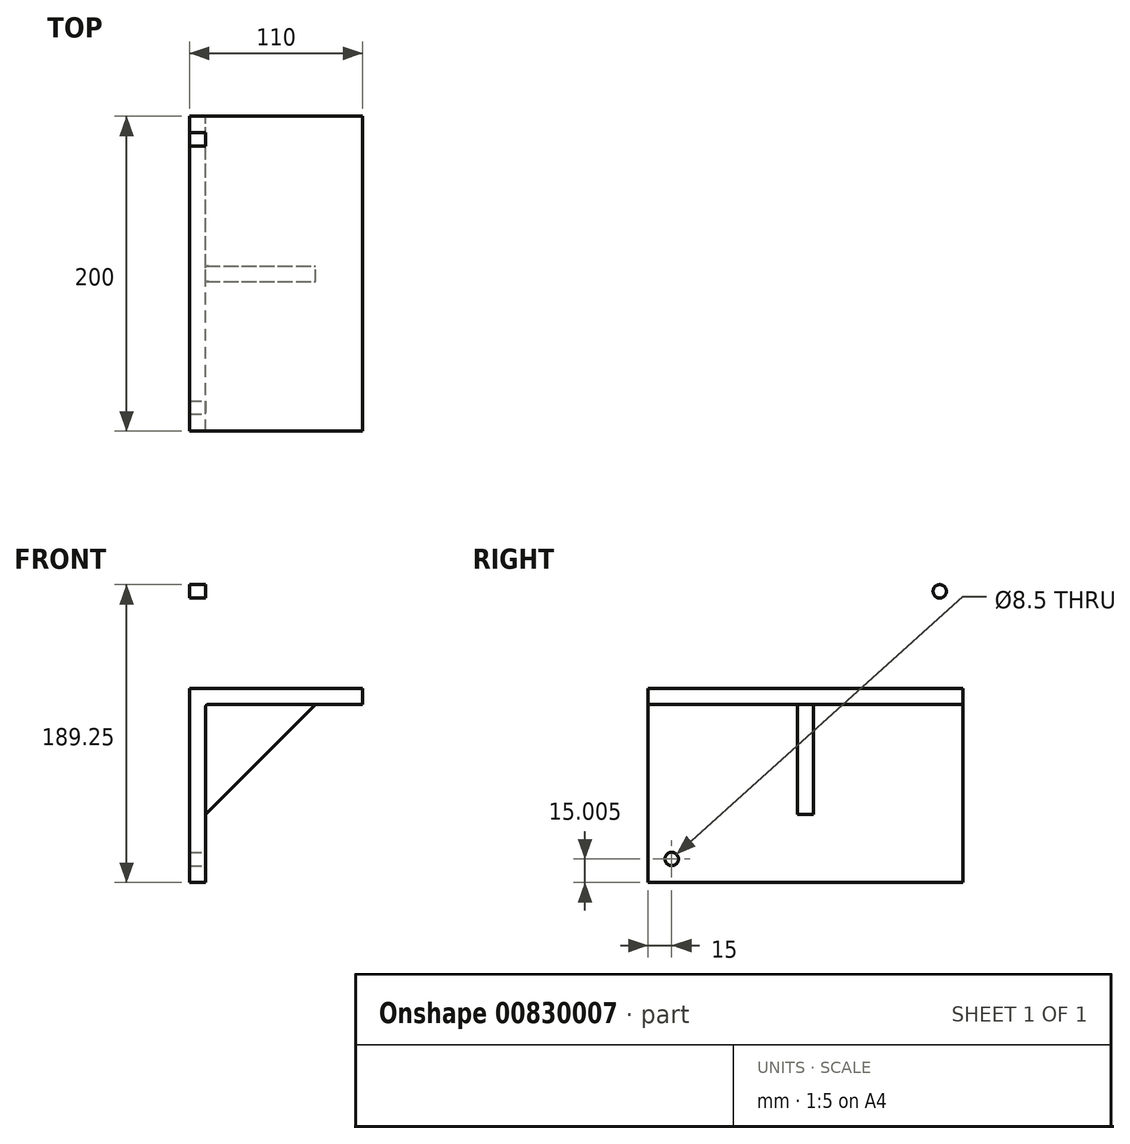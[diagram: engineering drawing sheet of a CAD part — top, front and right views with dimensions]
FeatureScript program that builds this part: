
annotation { "Feature Type Name" : "Feature", "Feature Type Description" : "" }
export const myFeature = defineFeature(function(context is Context, id is Id, definition is map)
    precondition{}
    {
        {
            var Q0;
            Q0=qCreatedBy(makeId("Front.planeOp"),FACE);
            var sketch = newSketch(context, id + "F0", { "sketchPlane" : qUnion([Q0])});
            skLineSegment(sketch, "E0", {"start": v(-10, 154.16) * mm, "end": v(0, 154.16) * mm});
            skLineSegment(sketch, "E1", {"start": v(0, 154.16) * mm, "end": v(0, 77.36) * mm});
            skLineSegment(sketch, "E2", {"start": v(-10, 154.16) * mm, "end": v(-10, -45.84) * mm});
            skLineSegment(sketch, "E3", {"start": v(-10, -45.84) * mm, "end": v(0, -45.84) * mm});
            skLineSegment(sketch, "E4", {"start": v(0, -45.84) * mm, "end": v(0, 67.36) * mm});
            skLineSegment(sketch, "E5", {"start": v(0, 77.36) * mm, "end": v(100, 77.36) * mm});
            skLineSegment(sketch, "E6", {"start": v(100, 77.36) * mm, "end": v(100, 67.36) * mm});
            skLineSegment(sketch, "E7", {"start": v(0, 67.36) * mm, "end": v(100, 67.36) * mm});
            skLineSegment(sketch, "E8", {"start": v(0, 67.36) * mm, "end": v(70, 67.36) * mm});
            skLineSegment(sketch, "E9", {"start": v(0, 67.36) * mm, "end": v(0, -2.64) * mm});
            skLineSegment(sketch, "E10", {"start": v(0, -2.64) * mm, "end": v(70, 67.36) * mm});
            skSolve(sketch);
        }
        {
            var Q0;
            Q0=makeQuery(id+"F0.imprint","IMPRINT",FACE,{"disambiguationData":[TD([[makeQuery(id+"F0.imprint","IMPRINT",EDGE,{"derivedFrom":sQuery(id+"F0.wireOp",EDGE,"E0")}),-1.0]])]});
            extrude(context, id + "F1", {"entities" : qUnion([Q0]), "depth" : 100 * mm, "offsetDistance" : 25 * mm});
        }
        {
            var Q0;
            Q0=makeQuery(id+"F0.imprint","IMPRINT",FACE,{"disambiguationData":[TD([[makeQuery(id+"F0.imprint","IMPRINT",EDGE,{"derivedFrom":sQuery(id+"F0.wireOp",EDGE,"E0")}),-1.0]])]});
            extrude(context, id + "F2", {"entities" : qUnion([Q0]), "operationType" : NewBodyOperationType.ADD, "oppositeDirection" : true, "depth" : 100 * mm, "offsetDistance" : 25 * mm});
        }
        {
            var Q0;
            {var subQ0=sQuery(id+"F0.wireOp",EDGE,"E10");Q0=makeQuery(id+"F0.imprint","IMPRINT",FACE,{"disambiguationData":[TD([[makeQuery(id+"F0.imprint","IMPRINT",EDGE,{"derivedFrom":subQ0}),1.0]])]});}
            extrude(context, id + "F3", {"entities" : qUnion([Q0]), "operationType" : NewBodyOperationType.ADD, "depth" : 5 * mm, "offsetDistance" : 25 * mm});
        }
        {
            var Q0;
            {var subQ0=sQuery(id+"F0.wireOp",EDGE,"E10");Q0=makeQuery(id+"F0.imprint","IMPRINT",FACE,{"disambiguationData":[TD([[makeQuery(id+"F0.imprint","IMPRINT",EDGE,{"derivedFrom":subQ0}),1.0]])]});}
            extrude(context, id + "F4", {"entities" : qUnion([Q0]), "operationType" : NewBodyOperationType.ADD, "oppositeDirection" : true, "depth" : 5 * mm, "offsetDistance" : 25 * mm});
        }
        {
            var Q0;
            {var subQ0=sQuery(id+"F0.wireOp",EDGE,"E1");Q0=makeQuery(id+"F2.boolean.opBoolean","MERGE",FACE,{"derivedFrom":[makeQuery(id+"F1.opExtrude","SWEPT_FACE",FACE,{"disambiguationData":[OSD([subQ0])]}),makeQuery(id+"F2.opExtrude","SWEPT_FACE",FACE,{"disambiguationData":[OSD([subQ0])]})]});}
            var sketch = newSketch(context, id + "F5", { "sketchPlane" : qUnion([Q0])});
            skCircle(sketch, "E11", {"center": v(-85.26, 139.16) * mm, "radius": 4.25 * mm});
            skCircle(sketch, "E12.MirrorC", {"center": v(85.26, 139.16) * mm, "radius": 4.25 * mm});
            skCircle(sketch, "E13", {"center": v(-85, -30.84) * mm, "radius": 4.25 * mm});
            skCircle(sketch, "E14.MirrorC", {"center": v(85, -30.84) * mm, "radius": 4.25 * mm});
            skSolve(sketch);
        }
        {
            var Q0;
            Q0=makeQuery(id+"F5.imprint","IMPRINT",FACE,{"disambiguationData":[TD([[makeQuery(id+"F5.imprint","IMPRINT",EDGE,{"derivedFrom":sQuery(id+"F5.wireOp",EDGE,"E12.MirrorC")}),-1.0]])]});
            var Q1;
            Q1=makeQuery(id+"F5.imprint","IMPRINT",FACE,{"disambiguationData":[TD([[makeQuery(id+"F5.imprint","IMPRINT",EDGE,{"derivedFrom":sQuery(id+"F5.wireOp",EDGE,"E11")}),1.0]])]});
            var Q2;
            Q2=makeQuery(id+"F5.imprint","IMPRINT",FACE,{"disambiguationData":[TD([[makeQuery(id+"F5.imprint","IMPRINT",EDGE,{"derivedFrom":sQuery(id+"F5.wireOp",EDGE,"E13")}),1.0]])]});
            var Q3;
            Q3=makeQuery(id+"F5.imprint","IMPRINT",FACE,{"disambiguationData":[TD([[makeQuery(id+"F5.imprint","IMPRINT",EDGE,{"derivedFrom":sQuery(id+"F5.wireOp",EDGE,"E14.MirrorC")}),-1.0]])]});
            extrude(context, id + "F6", {"entities" : qUnion([Q0, Q1, Q2, Q3]), "operationType" : NewBodyOperationType.REMOVE, "oppositeDirection" : true, "depth" : 10 * mm, "offsetDistance" : 25 * mm});
        }
        {
            var Q0;
            {var subQ0=sQuery(id+"F0.wireOp",EDGE,"E7");var subQ1=sQuery(id+"F0.wireOp",EDGE,"E4");Q0=makeQuery(id+"F3.boolean.opBoolean","SPLIT",EDGE,{"disambiguationData":[TD([makeQuery(id+"F3.opExtrude","CAP_FACE",FACE,{"disambiguationData":[OSD([subQ1,subQ0,sQuery(id+"F0.wireOp",EDGE,"E10")])],"isStart":false})])],"derivedFrom":makeQuery(id+"F2.boolean.opBoolean","MERGE",EDGE,{"derivedFrom":[makeQuery(id+"F1.opExtrude","SWEPT_EDGE",EDGE,{"disambiguationData":[OSD([subQ1,subQ0])]}),makeQuery(id+"F2.opExtrude","SWEPT_EDGE",EDGE,{"disambiguationData":[OSD([subQ1,subQ0])]})]})});}
            var Q1;
            {var subQ0=sQuery(id+"F0.wireOp",EDGE,"E4");var subQ1=sQuery(id+"F0.wireOp",EDGE,"E7");Q1=makeQuery(id+"F3.boolean.opBoolean","SPLIT",EDGE,{"disambiguationData":[TD([makeQuery(id+"F3.opExtrude","CAP_FACE",FACE,{"disambiguationData":[OSD([subQ0,subQ1,sQuery(id+"F0.wireOp",EDGE,"E10")])],"isStart":true})])],"derivedFrom":makeQuery(id+"F2.boolean.opBoolean","MERGE",EDGE,{"derivedFrom":[makeQuery(id+"F1.opExtrude","SWEPT_EDGE",EDGE,{"disambiguationData":[OSD([subQ0,subQ1])]}),makeQuery(id+"F2.opExtrude","SWEPT_EDGE",EDGE,{"disambiguationData":[OSD([subQ0,subQ1])]})]})});}
            var Q2;
            Q2=makeQuery(id+"F4.opExtrude","CAP_EDGE",EDGE,{"disambiguationData":[OSD([sQuery(id+"F0.wireOp",EDGE,"E4")])],"isStart":false});
            var Q3;
            Q3=makeQuery(id+"F4.opExtrude","CAP_EDGE",EDGE,{"disambiguationData":[OSD([sQuery(id+"F0.wireOp",EDGE,"E7")])],"isStart":false});
            var Q4;
            Q4=makeQuery(id+"F3.opExtrude","CAP_EDGE",EDGE,{"disambiguationData":[OSD([sQuery(id+"F0.wireOp",EDGE,"E7")])],"isStart":false});
            var Q5;
            Q5=makeQuery(id+"F3.opExtrude","CAP_EDGE",EDGE,{"disambiguationData":[OSD([sQuery(id+"F0.wireOp",EDGE,"E4")])],"isStart":false});
            var Q6;
            {var subQ0=sQuery(id+"F0.wireOp",EDGE,"E10");var subQ1=sQuery(id+"F0.wireOp",EDGE,"E4");Q6=makeQuery(id+"F4.boolean.opBoolean","MERGE",EDGE,{"derivedFrom":[makeQuery(id+"F3.opExtrude","SWEPT_EDGE",EDGE,{"disambiguationData":[OSD([subQ1,subQ0])]}),makeQuery(id+"F4.opExtrude","SWEPT_EDGE",EDGE,{"disambiguationData":[OSD([subQ1,subQ0])]})]});}
            var Q7;
            {var subQ0=sQuery(id+"F0.wireOp",EDGE,"E10");var subQ1=sQuery(id+"F0.wireOp",EDGE,"E7");Q7=makeQuery(id+"F4.boolean.opBoolean","MERGE",EDGE,{"derivedFrom":[makeQuery(id+"F3.opExtrude","SWEPT_EDGE",EDGE,{"disambiguationData":[OSD([subQ1,subQ0])]}),makeQuery(id+"F4.opExtrude","SWEPT_EDGE",EDGE,{"disambiguationData":[OSD([subQ1,subQ0])]})]});}
            var Q8;
            {var subQ0=sQuery(id+"F0.wireOp",EDGE,"E5");var subQ1=sQuery(id+"F0.wireOp",EDGE,"E1");Q8=makeQuery(id+"F2.boolean.opBoolean","MERGE",EDGE,{"derivedFrom":[makeQuery(id+"F1.opExtrude","SWEPT_EDGE",EDGE,{"disambiguationData":[OSD([subQ1,subQ0])]}),makeQuery(id+"F2.opExtrude","SWEPT_EDGE",EDGE,{"disambiguationData":[OSD([subQ1,subQ0])]})]});}
            fillet(context, id + "F7", {"entities" : qUnion([Q0, Q1, Q2, Q3, Q4, Q5, Q6, Q7, Q8]), "radius" : 2 * mm, "tangentPropagation" : true, "allowEdgeOverflow" : false});
        }
    });
